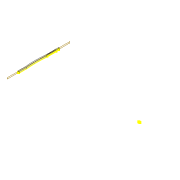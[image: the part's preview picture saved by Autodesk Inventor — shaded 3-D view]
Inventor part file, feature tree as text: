
AUTODESK INVENTOR PART (.ipt)
format: ipt  version: 2022 (Build 260153000, 153)  size: 121,856 bytes
history: native  units: mm
features: sketch x3, extrude x1, projected_geometry x1
ambient origin geometry x8: Origin, YZ Plane, XZ Plane, XY Plane, X Axis, Y Axis, Z Axis, Center Point
bodies: Solid1 (feature_tree)
feature tree (5):
  extrude  "Extrusion1"  Depth=8.0mm
  sketch  "Sketch2"  dims[d2=3.0mm]
  sketch  "Sketch3"  dims[d3=3.0mm d4=8.0mm d5=0.0mm d10=3.0mm d11=19.5mm d12=80.0mm d13=85.0mm d14=220.0mm d15=700.0mm d16=700.0mm]
  sketch  "Sketch1"  dims[d0=270.69mm d1=8.0mm]
  projected_geometry  "Projected Loop1"
